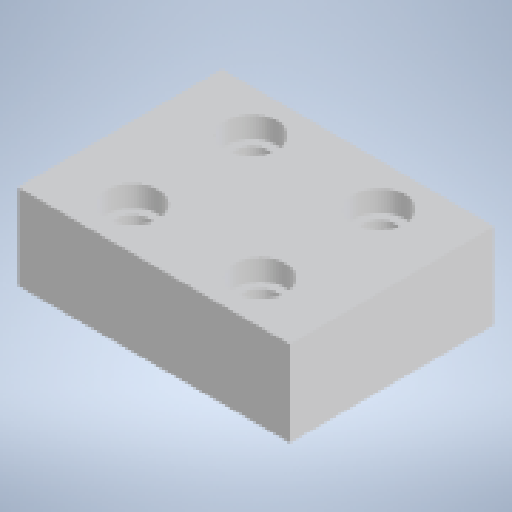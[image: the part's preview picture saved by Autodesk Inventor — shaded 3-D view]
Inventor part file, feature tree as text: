
AUTODESK INVENTOR PART (.ipt)
format: ipt  version: 2024 (Build 280153000, 153)  size: 154,624 bytes
history: native  units: mm
features: extrude x2
ambient origin geometry x8: Origin, YZ Plane, XZ Plane, XY Plane, X Axis, Y Axis, Z Axis, Center Point
bodies: Solid1 (feature_tree)
feature tree (2):
  extrude  "Extrusion1"  Depth=32.0mm
  extrude  "Extrusion2"  Depth=24.0mm
